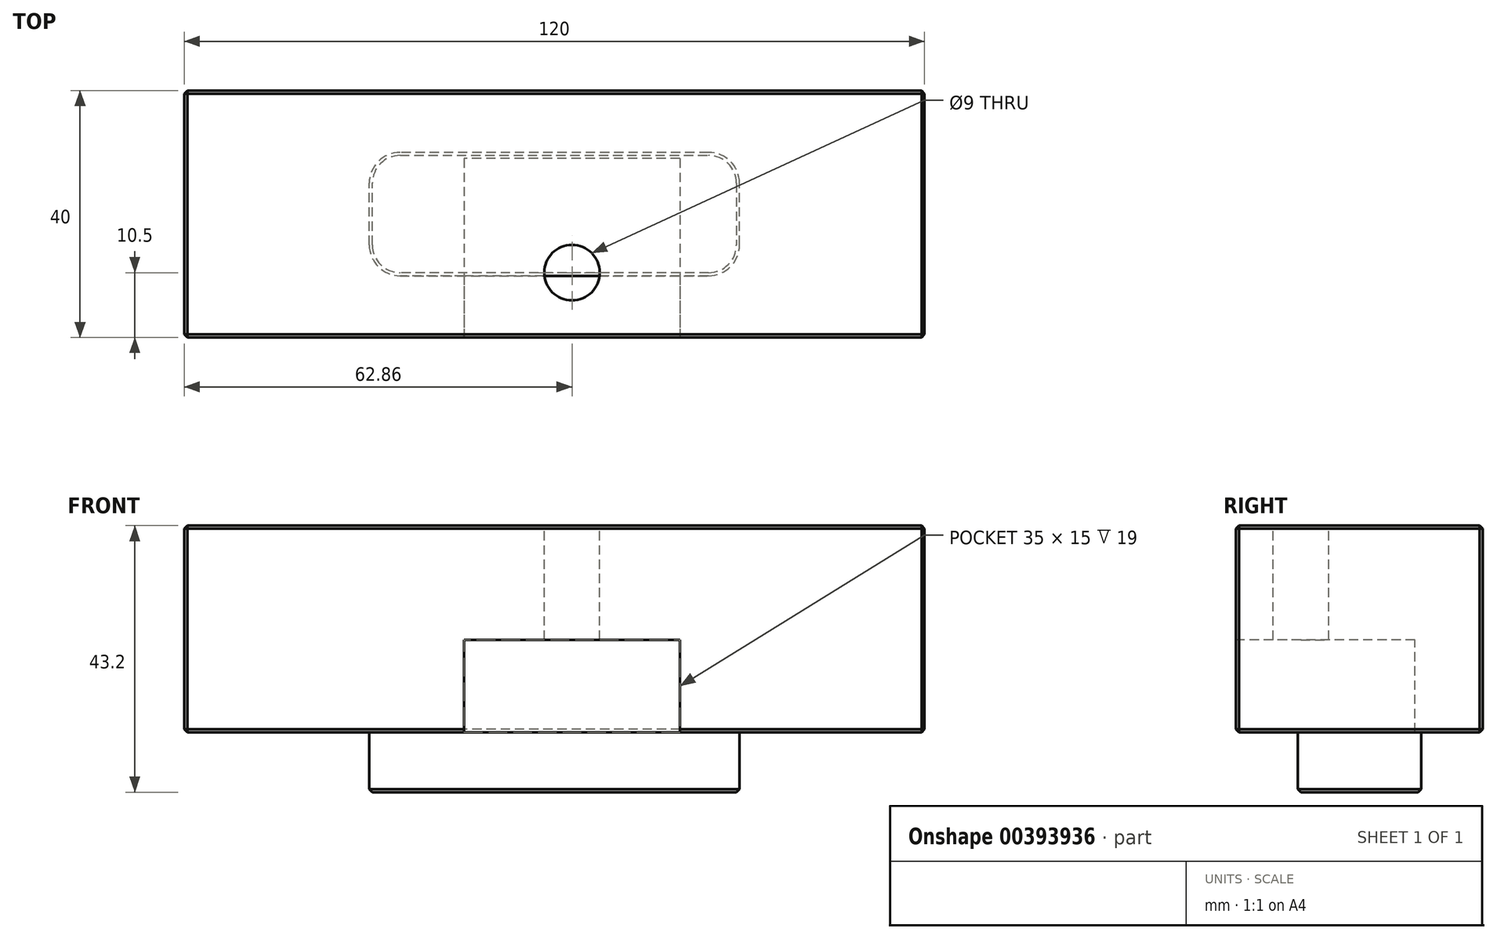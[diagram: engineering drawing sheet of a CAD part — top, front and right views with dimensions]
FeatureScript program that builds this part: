
annotation { "Feature Type Name" : "Feature", "Feature Type Description" : "" }
export const myFeature = defineFeature(function(context is Context, id is Id, definition is map)
    precondition{}
    {
        {
            var Q0;
            Q0=qCreatedBy(makeId("Front.planeOp"),FACE);
            var sketch = newSketch(context, id + "F0", { "sketchPlane" : qUnion([Q0])});
            skLineSegment(sketch, "E0.bottom", {"start": v(57.14, -16.75) * mm, "end": v(-62.86, -16.75) * mm});
            skLineSegment(sketch, "E0.top", {"start": v(57.14, 16.75) * mm, "end": v(-62.86, 16.75) * mm});
            skLineSegment(sketch, "E0.left", {"start": v(57.14, -16.75) * mm, "end": v(57.14, 16.75) * mm});
            skLineSegment(sketch, "E0.right", {"start": v(-62.86, -16.75) * mm, "end": v(-62.86, 16.75) * mm});
            skPoint(sketch, "E0.middle", {"position": v(-2.86, 0) * mm});
            skSolve(sketch);
        }
        {
            var Q0;
            Q0 = qSketchRegion(id + "F0", true);
            extrude(context, id + "F1", {"entities" : qUnion([Q0]), "oppositeDirection" : true, "offsetDistance" : 25 * mm, "depth" : 40 * mm});
        }
        {
            var Q0;
            Q0=makeQuery(id+"F1.opExtrude","SWEPT_FACE",FACE,{"disambiguationData":[OSD([sQuery(id+"F0.wireOp",EDGE,"E0.bottom")])]});
            var sketch = newSketch(context, id + "F2", { "sketchPlane" : qUnion([Q0])});
            skSolve(sketch);
        }
        {
            var Q0;
            {var subQ0=sQuery(id+"F0.wireOp",EDGE,"E0.bottom");Q0=makeQuery(id+"F2.imprint","IMPRINT",FACE,{"disambiguationData":[TD([[makeQuery(id+"F2.imprint","IMPRINT",EDGE,{"derivedFrom":makeQuery(id+"F1.opExtrude","CAP_EDGE",EDGE,{"disambiguationData":[OSD([subQ0])],"isStart":true})}),1.0]])]});}
            var sketch = newSketch(context, id + "F3", { "sketchPlane" : qUnion([Q0])});
            skLineSegment(sketch, "E1.bottom", {"start": v(22.14, -10) * mm, "end": v(-27.86, -10) * mm});
            skLineSegment(sketch, "E1.top", {"start": v(22.14, -30) * mm, "end": v(-27.86, -30) * mm});
            skLineSegment(sketch, "E1.left", {"start": v(27.14, -15) * mm, "end": v(27.14, -25) * mm});
            skLineSegment(sketch, "E1.right", {"start": v(-32.86, -15) * mm, "end": v(-32.86, -25) * mm});
            skPoint(sketch, "E1.middle", {"position": v(-2.86, -20) * mm});
            skPoint(sketch, "E2.visualSharp", {"position": v(-32.86, -30) * mm});
            skArc(sketch, "E2.filletArc", {"start": v(-32.86, -25) * mm, "mid": v(-31.4, -28.54) * mm, "end": v(-27.86, -30) * mm});
            skPoint(sketch, "E3.visualSharp", {"position": v(-32.86, -10) * mm});
            skArc(sketch, "E3.filletArc", {"start": v(-27.86, -10) * mm, "mid": v(-31.4, -11.46) * mm, "end": v(-32.86, -15) * mm});
            skPoint(sketch, "E4.visualSharp", {"position": v(27.14, -10) * mm});
            skArc(sketch, "E4.filletArc", {"start": v(27.14, -15) * mm, "mid": v(25.68, -11.46) * mm, "end": v(22.14, -10) * mm});
            skPoint(sketch, "E5.visualSharp", {"position": v(27.14, -30) * mm});
            skArc(sketch, "E5.filletArc", {"start": v(22.14, -30) * mm, "mid": v(25.68, -28.54) * mm, "end": v(27.14, -25) * mm});
            skSolve(sketch);
        }
        {
            var Q0;
            Q0 = qSketchRegion(id + "F3", true);
            extrude(context, id + "F4", {"entities" : qUnion([Q0]), "operationType" : NewBodyOperationType.ADD, "depth" : 9.7 * mm});
        }
        {
            var Q0;
            Q0=makeQuery(id+"F1.opExtrude","SWEPT_FACE",FACE,{"disambiguationData":[OSD([sQuery(id+"F0.wireOp",EDGE,"E0.top")])]});
            var sketch = newSketch(context, id + "F5", { "sketchPlane" : qUnion([Q0])});
            skCircle(sketch, "E6", {"center": v(0, 10.5) * mm, "radius": 4.5 * mm});
            skSolve(sketch);
        }
        {
            var Q0;
            Q0 = qSketchRegion(id + "F5", true);
            extrude(context, id + "F6", {"entities" : qUnion([Q0]), "operationType" : NewBodyOperationType.REMOVE, "oppositeDirection" : true, "depth" : 33.5 * mm, "offsetDistance" : 25 * mm});
        }
        {
            var Q0;
            Q0=makeQuery(id+"F1.opExtrude","CAP_FACE",FACE,{"disambiguationData":[OSD([sQuery(id+"F0.wireOp",EDGE,"E0.bottom"),sQuery(id+"F0.wireOp",EDGE,"E0.top"),sQuery(id+"F0.wireOp",EDGE,"E0.left"),sQuery(id+"F0.wireOp",EDGE,"E0.right")])],"isStart":true});
            var sketch = newSketch(context, id + "F7", { "sketchPlane" : qUnion([Q0])});
            skLineSegment(sketch, "E7.bottom", {"start": v(-17.5, -16.75) * mm, "end": v(17.5, -16.75) * mm});
            skLineSegment(sketch, "E7.top", {"start": v(-17.5, -1.75) * mm, "end": v(17.5, -1.75) * mm});
            skLineSegment(sketch, "E7.left", {"start": v(-17.5, -16.75) * mm, "end": v(-17.5, -1.75) * mm});
            skLineSegment(sketch, "E7.right", {"start": v(17.5, -16.75) * mm, "end": v(17.5, -1.75) * mm});
            skSolve(sketch);
        }
        {
            var Q0;
            Q0 = qSketchRegion(id + "F7", true);
            extrude(context, id + "F8", {"entities" : qUnion([Q0]), "operationType" : NewBodyOperationType.REMOVE, "oppositeDirection" : true, "depth" : 29 * mm, "offsetDistance" : 25 * mm});
        }
        {
            var Q0;
            Q0=makeQuery(id+"F1.opExtrude","CAP_EDGE",EDGE,{"disambiguationData":[OSD([sQuery(id+"F0.wireOp",EDGE,"E0.top")])],"isStart":true});
            var Q1;
            Q1=makeQuery(id+"F1.opExtrude","SWEPT_EDGE",EDGE,{"disambiguationData":[OSD([sQuery(id+"F0.wireOp",EDGE,"E0.top"),sQuery(id+"F0.wireOp",EDGE,"E0.left")])]});
            var Q2;
            Q2=makeQuery(id+"F1.opExtrude","CAP_EDGE",EDGE,{"disambiguationData":[OSD([sQuery(id+"F0.wireOp",EDGE,"E0.top")])],"isStart":false});
            var Q3;
            Q3=makeQuery(id+"F1.opExtrude","SWEPT_EDGE",EDGE,{"disambiguationData":[OSD([sQuery(id+"F0.wireOp",EDGE,"E0.top"),sQuery(id+"F0.wireOp",EDGE,"E0.right")])]});
            var Q4;
            Q4=makeQuery(id+"F1.opExtrude","CAP_EDGE",EDGE,{"disambiguationData":[OSD([sQuery(id+"F0.wireOp",EDGE,"E0.right")])],"isStart":true});
            var Q5;
            Q5=makeQuery(id+"F1.opExtrude","CAP_EDGE",EDGE,{"disambiguationData":[OSD([sQuery(id+"F0.wireOp",EDGE,"E0.left")])],"isStart":true});
            var Q6;
            Q6=makeQuery(id+"F1.opExtrude","CAP_EDGE",EDGE,{"disambiguationData":[OSD([sQuery(id+"F0.wireOp",EDGE,"E0.left")])],"isStart":false});
            var Q7;
            Q7=makeQuery(id+"F1.opExtrude","CAP_EDGE",EDGE,{"disambiguationData":[OSD([sQuery(id+"F0.wireOp",EDGE,"E0.right")])],"isStart":false});
            var Q8;
            Q8=makeQuery(id+"F1.opExtrude","SWEPT_EDGE",EDGE,{"disambiguationData":[OSD([sQuery(id+"F0.wireOp",EDGE,"E0.bottom"),sQuery(id+"F0.wireOp",EDGE,"E0.right")])]});
            var Q9;
            {var subQ0=sQuery(id+"F0.wireOp",EDGE,"E0.bottom");var subQ1=sQuery(id+"F0.wireOp",EDGE,"E0.right");Q9=makeQuery(id+"F8.boolean.opBoolean","SPLIT",EDGE,{"disambiguationData":[TD([makeQuery(id+"F1.opExtrude","SWEPT_FACE",FACE,{"disambiguationData":[OSD([subQ1])]})])],"derivedFrom":makeQuery(id+"F1.opExtrude","CAP_EDGE",EDGE,{"disambiguationData":[OSD([subQ0])],"isStart":true})});}
            var Q10;
            Q10=makeQuery(id+"F8.boolean.opBoolean","COPY",EDGE,{"derivedFrom":makeQuery(id+"F8.opExtrude","CAP_EDGE",EDGE,{"disambiguationData":[OSD([sQuery(id+"F7.wireOp",EDGE,"E7.left")])],"isStart":true})});
            var Q11;
            Q11=makeQuery(id+"F8.boolean.opBoolean","COPY",EDGE,{"derivedFrom":makeQuery(id+"F8.opExtrude","CAP_EDGE",EDGE,{"disambiguationData":[OSD([sQuery(id+"F7.wireOp",EDGE,"E7.top")])],"isStart":true})});
            var Q12;
            Q12=makeQuery(id+"F8.boolean.opBoolean","COPY",EDGE,{"derivedFrom":makeQuery(id+"F8.opExtrude","CAP_EDGE",EDGE,{"disambiguationData":[OSD([sQuery(id+"F7.wireOp",EDGE,"E7.right")])],"isStart":true})});
            var Q13;
            {var subQ0=sQuery(id+"F0.wireOp",EDGE,"E0.bottom");var subQ1=sQuery(id+"F0.wireOp",EDGE,"E0.left");Q13=makeQuery(id+"F8.boolean.opBoolean","SPLIT",EDGE,{"disambiguationData":[TD([makeQuery(id+"F1.opExtrude","SWEPT_FACE",FACE,{"disambiguationData":[OSD([subQ1])]})])],"derivedFrom":makeQuery(id+"F1.opExtrude","CAP_EDGE",EDGE,{"disambiguationData":[OSD([subQ0])],"isStart":true})});}
            var Q14;
            Q14=makeQuery(id+"F1.opExtrude","SWEPT_EDGE",EDGE,{"disambiguationData":[OSD([sQuery(id+"F0.wireOp",EDGE,"E0.bottom"),sQuery(id+"F0.wireOp",EDGE,"E0.left")])]});
            var Q15;
            Q15=makeQuery(id+"F1.opExtrude","CAP_EDGE",EDGE,{"disambiguationData":[OSD([sQuery(id+"F0.wireOp",EDGE,"E0.bottom")])],"isStart":false});
            chamfer(context, id + "F9", {"entities" : qUnion([Q0, Q1, Q2, Q3, Q4, Q5, Q6, Q7, Q8, Q9, Q10, Q11, Q12, Q13, Q14, Q15]), "width" : 0.5 * mm, "tangentPropagation" : true});
        }
        {
            var Q0;
            Q0=makeQuery(id+"F4.opExtrude","CAP_EDGE",EDGE,{"disambiguationData":[OSD([sQuery(id+"F3.wireOp",EDGE,"E1.bottom")])],"isStart":false});
            chamfer(context, id + "F10", {"entities" : qUnion([Q0]), "width" : 0.5 * mm, "tangentPropagation" : true});
        }
    });
